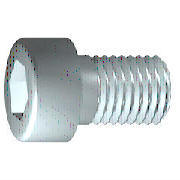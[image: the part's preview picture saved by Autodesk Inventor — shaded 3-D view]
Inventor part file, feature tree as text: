
AUTODESK INVENTOR PART (.ipt)
format: ipt  version: 2013 (Build 170138000, 138)  size: 176,640 bytes
history: native  units: mm (DEFAULTED — no unit token found)
features: sketch x2, extrude x1, plane x1, fillet x1
ambient origin geometry x7: Origin, YZ Plane, XY Plane, X Axis, Y Axis, Z Axis, Center Point
bodies: Solid1 (feature_tree), Body (feature_tree)
feature tree (5):
  extrude  "Slot"  Depth=0.306825mm
  plane  "Work Plane1"
  fillet  "Fillet2"  Radius=3.0mm
  sketch  "Sketch1"  dims[d1=18.0mm d2=0.306825mm d3=3.0mm]
  sketch  "Sketch2"  dims[d4=1.5mm d5=60.0deg d6=3.0mm d7=3.0mm d8=2.886751mm d9=5.5mm d10=90.0deg d11=10.0mm d12=0.0mm d13=18.0mm d14=0.0mm d15=0.306725mm d16=0.306725mm d17=0.3mm d19=0.0mm d26=65.0mm d27=45.0deg d28=0.0mm d29=0.0mm d30=0.1mm]
